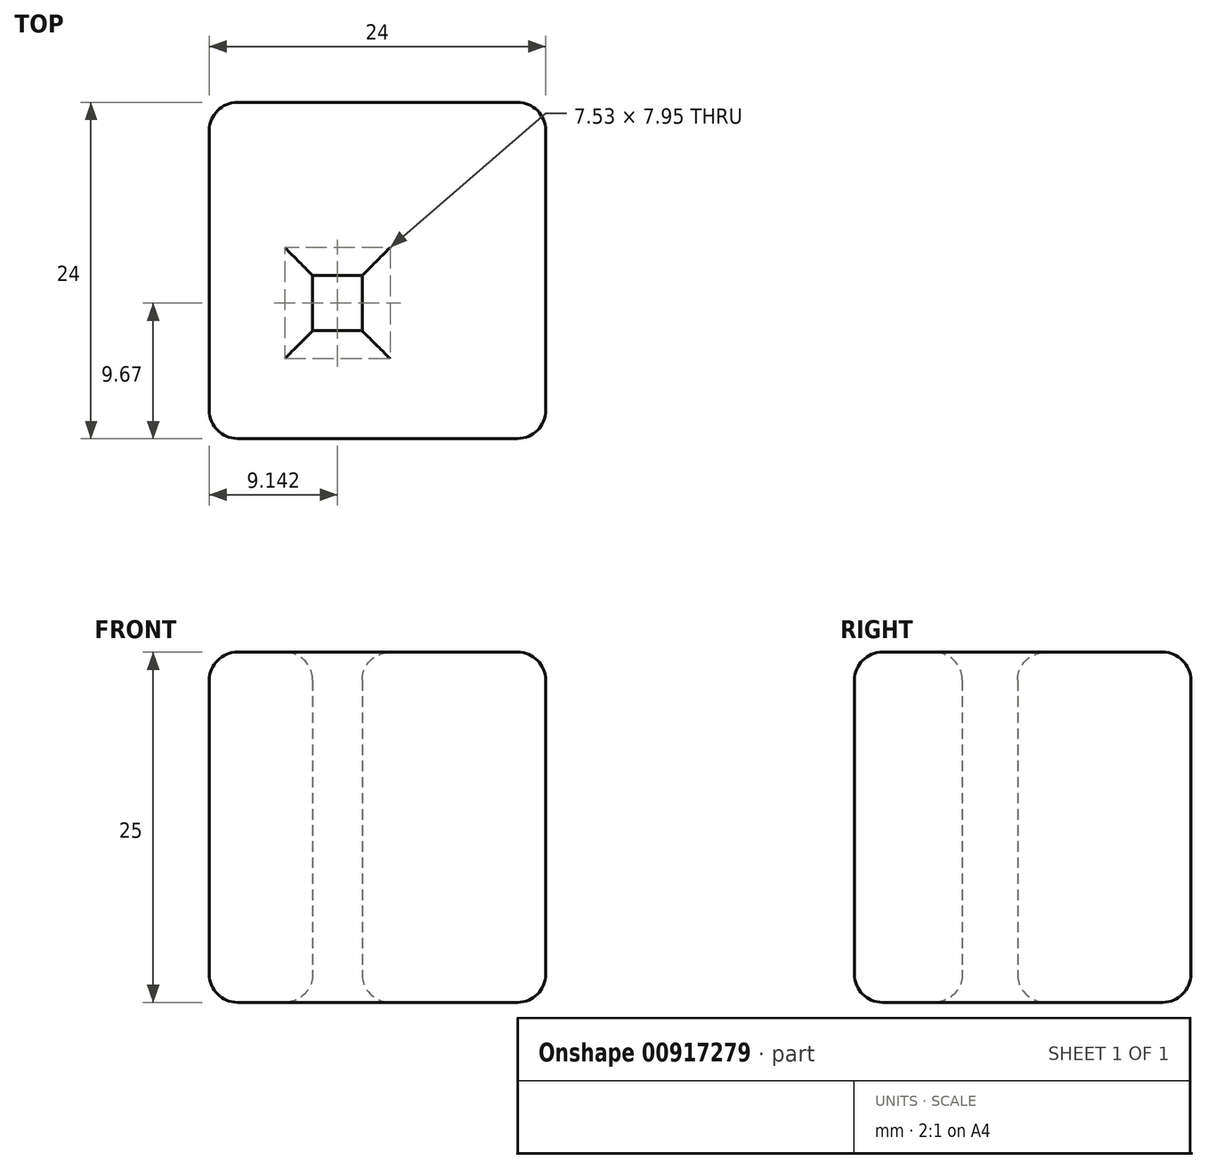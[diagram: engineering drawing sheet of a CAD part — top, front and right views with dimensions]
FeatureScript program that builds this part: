
annotation { "Feature Type Name" : "Feature", "Feature Type Description" : "" }
export const myFeature = defineFeature(function(context is Context, id is Id, definition is map)
    precondition{}
    {
        {
            var Q0;
            Q0=qCreatedBy(makeId("Top.planeOp"),FACE);
            var sketch = newSketch(context, id + "F0", { "sketchPlane" : qUnion([Q0])});
            skLineSegment(sketch, "E0.bottom", {"start": v(-44.68, -6.29) * mm, "end": v(-20.68, -6.29) * mm});
            skLineSegment(sketch, "E0.top", {"start": v(-44.68, -30.29) * mm, "end": v(-20.68, -30.29) * mm});
            skLineSegment(sketch, "E0.left", {"start": v(-44.68, -6.29) * mm, "end": v(-44.68, -30.29) * mm});
            skLineSegment(sketch, "E0.right", {"start": v(-20.68, -6.29) * mm, "end": v(-20.68, -30.29) * mm});
            skLineSegment(sketch, "E1.bottom", {"start": v(-33.77, -18.65) * mm, "end": v(-37.3, -18.65) * mm});
            skLineSegment(sketch, "E1.top", {"start": v(-33.77, -22.6) * mm, "end": v(-37.3, -22.6) * mm});
            skLineSegment(sketch, "E1.left", {"start": v(-33.77, -18.65) * mm, "end": v(-33.77, -22.6) * mm});
            skLineSegment(sketch, "E1.right", {"start": v(-37.3, -18.65) * mm, "end": v(-37.3, -22.6) * mm});
            skSolve(sketch);
        }
        {
            var Q0;
            Q0=makeQuery(id+"F0.imprint","IMPRINT",FACE,{"disambiguationData":[TD([[makeQuery(id+"F0.imprint","IMPRINT",EDGE,{"derivedFrom":sQuery(id+"F0.wireOp",EDGE,"E0.bottom")}),-1.0]])]});
            extrude(context, id + "F1", {"entities" : qUnion([Q0]), "depth" : 25 * mm, "offsetDistance" : 25 * mm});
        }
        {
            var Q0;
            Q0=makeQuery(id+"F1.opExtrude","SWEPT_EDGE",EDGE,{"disambiguationData":[OSD([sQuery(id+"F0.wireOp",EDGE,"E0.bottom"),sQuery(id+"F0.wireOp",EDGE,"E0.left")])]});
            var Q1;
            Q1=makeQuery(id+"F1.opExtrude","CAP_EDGE",EDGE,{"disambiguationData":[OSD([sQuery(id+"F0.wireOp",EDGE,"E0.bottom")])],"isStart":false});
            var Q2;
            Q2=makeQuery(id+"F1.opExtrude","SWEPT_EDGE",EDGE,{"disambiguationData":[OSD([sQuery(id+"F0.wireOp",EDGE,"E0.bottom"),sQuery(id+"F0.wireOp",EDGE,"E0.right")])]});
            var Q3;
            Q3=makeQuery(id+"F1.opExtrude","CAP_EDGE",EDGE,{"disambiguationData":[OSD([sQuery(id+"F0.wireOp",EDGE,"E0.bottom")])],"isStart":true});
            var Q4;
            Q4=makeQuery(id+"F1.opExtrude","SWEPT_FACE",FACE,{"disambiguationData":[OSD([sQuery(id+"F0.wireOp",EDGE,"E0.left")])]});
            var Q5;
            Q5=makeQuery(id+"F1.opExtrude","CAP_EDGE",EDGE,{"disambiguationData":[OSD([sQuery(id+"F0.wireOp",EDGE,"E0.top")])],"isStart":false});
            var Q6;
            Q6=makeQuery(id+"F1.opExtrude","CAP_EDGE",EDGE,{"disambiguationData":[OSD([sQuery(id+"F0.wireOp",EDGE,"E0.right")])],"isStart":false});
            var Q7;
            Q7=makeQuery(id+"F1.opExtrude","SWEPT_EDGE",EDGE,{"disambiguationData":[OSD([sQuery(id+"F0.wireOp",EDGE,"E0.top"),sQuery(id+"F0.wireOp",EDGE,"E0.right")])]});
            var Q8;
            Q8=makeQuery(id+"F1.opExtrude","CAP_EDGE",EDGE,{"disambiguationData":[OSD([sQuery(id+"F0.wireOp",EDGE,"E0.right")])],"isStart":true});
            var Q9;
            Q9=makeQuery(id+"F1.opExtrude","CAP_EDGE",EDGE,{"disambiguationData":[OSD([sQuery(id+"F0.wireOp",EDGE,"E0.top")])],"isStart":true});
            var Q10;
            Q10=makeQuery(id+"F1.opExtrude","SWEPT_FACE",FACE,{"disambiguationData":[OSD([sQuery(id+"F0.wireOp",EDGE,"E0.top")])]});
            var Q11;
            Q11=makeQuery(id+"F1.opExtrude","CAP_EDGE",EDGE,{"disambiguationData":[OSD([sQuery(id+"F0.wireOp",EDGE,"E0.left")])],"isStart":false});
            fillet(context, id + "F2", {"entities" : qUnion([Q0, Q1, Q2, Q3, Q4, Q5, Q6, Q7, Q8, Q9, Q10, Q11]), "radius" : 2 * mm, "tangentPropagation" : true, "allowEdgeOverflow" : false});
        }
        {
            var Q0;
            Q0=makeQuery(id+"F1.opExtrude","CAP_EDGE",EDGE,{"disambiguationData":[OSD([sQuery(id+"F0.wireOp",EDGE,"E1.left")])],"isStart":false});
            var Q1;
            Q1=makeQuery(id+"F1.opExtrude","CAP_EDGE",EDGE,{"disambiguationData":[OSD([sQuery(id+"F0.wireOp",EDGE,"E1.top")])],"isStart":true});
            var Q2;
            Q2=makeQuery(id+"F1.opExtrude","CAP_EDGE",EDGE,{"disambiguationData":[OSD([sQuery(id+"F0.wireOp",EDGE,"E1.bottom")])],"isStart":false});
            var Q3;
            Q3=makeQuery(id+"F1.opExtrude","CAP_EDGE",EDGE,{"disambiguationData":[OSD([sQuery(id+"F0.wireOp",EDGE,"E1.right")])],"isStart":false});
            var Q4;
            Q4=makeQuery(id+"F1.opExtrude","CAP_EDGE",EDGE,{"disambiguationData":[OSD([sQuery(id+"F0.wireOp",EDGE,"E1.top")])],"isStart":false});
            var Q5;
            Q5=makeQuery(id+"F1.opExtrude","CAP_EDGE",EDGE,{"disambiguationData":[OSD([sQuery(id+"F0.wireOp",EDGE,"E1.right")])],"isStart":true});
            var Q6;
            Q6=makeQuery(id+"F1.opExtrude","CAP_EDGE",EDGE,{"disambiguationData":[OSD([sQuery(id+"F0.wireOp",EDGE,"E1.bottom")])],"isStart":true});
            var Q7;
            Q7=makeQuery(id+"F1.opExtrude","CAP_EDGE",EDGE,{"disambiguationData":[OSD([sQuery(id+"F0.wireOp",EDGE,"E1.left")])],"isStart":true});
            fillet(context, id + "F3", {"entities" : qUnion([Q0, Q1, Q2, Q3, Q4, Q5, Q6, Q7]), "radius" : 2 * mm, "tangentPropagation" : true, "allowEdgeOverflow" : false});
        }
    });
